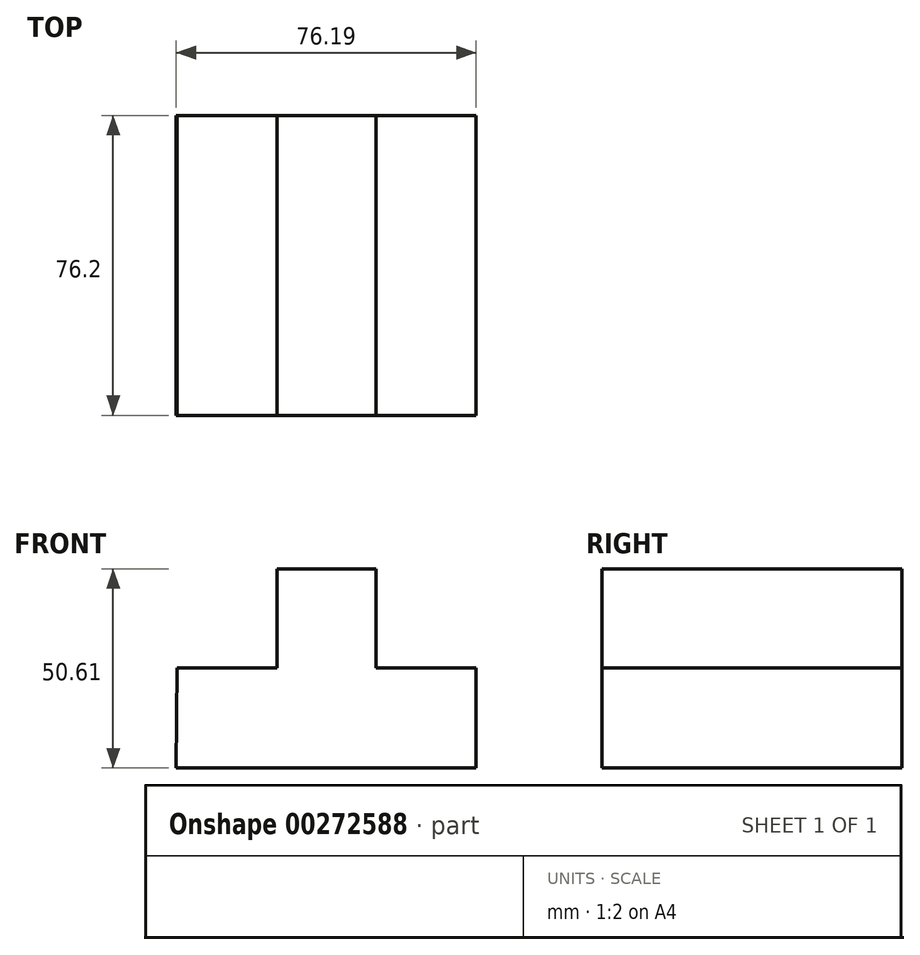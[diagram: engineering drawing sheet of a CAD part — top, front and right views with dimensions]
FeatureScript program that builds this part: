
annotation { "Feature Type Name" : "Feature", "Feature Type Description" : "" }
export const myFeature = defineFeature(function(context is Context, id is Id, definition is map)
    precondition{}
    {
        {
            var Q0;
            Q0=qCreatedBy(makeId("Front.planeOp"),FACE);
            var sketch = newSketch(context, id + "F0", { "sketchPlane" : qUnion([Q0])});
            skLineSegment(sketch, "E0", {"start": v(-52.51, -37.05) * mm, "end": v(23.68, -37.05) * mm});
            skLineSegment(sketch, "E1", {"start": v(23.68, -37.05) * mm, "end": v(23.68, -11.65) * mm});
            skLineSegment(sketch, "E2", {"start": v(23.68, -11.65) * mm, "end": v(-1.72, -11.65) * mm});
            skLineSegment(sketch, "E3", {"start": v(-1.72, -11.65) * mm, "end": v(-1.72, 13.56) * mm});
            skLineSegment(sketch, "E4", {"start": v(-1.72, 13.56) * mm, "end": v(-26.92, 13.56) * mm});
            skLineSegment(sketch, "E5", {"start": v(-26.92, 13.56) * mm, "end": v(-26.92, -11.65) * mm});
            skLineSegment(sketch, "E6", {"start": v(-26.92, -11.65) * mm, "end": v(-52.32, -11.65) * mm});
            skLineSegment(sketch, "E7", {"start": v(-52.32, -11.65) * mm, "end": v(-52.51, -37.05) * mm});
            skSolve(sketch);
        }
        {
            var Q0;
            Q0=makeQuery(id+"F0.imprint","IMPRINT",FACE,{"disambiguationData":[TD([[makeQuery(id+"F0.imprint","IMPRINT",EDGE,{"derivedFrom":sQuery(id+"F0.wireOp",EDGE,"E0")}),1.0]])]});
            extrude(context, id + "F1", {"entities" : qUnion([Q0]), "depth" : 76.2 * mm});
        }
    });
